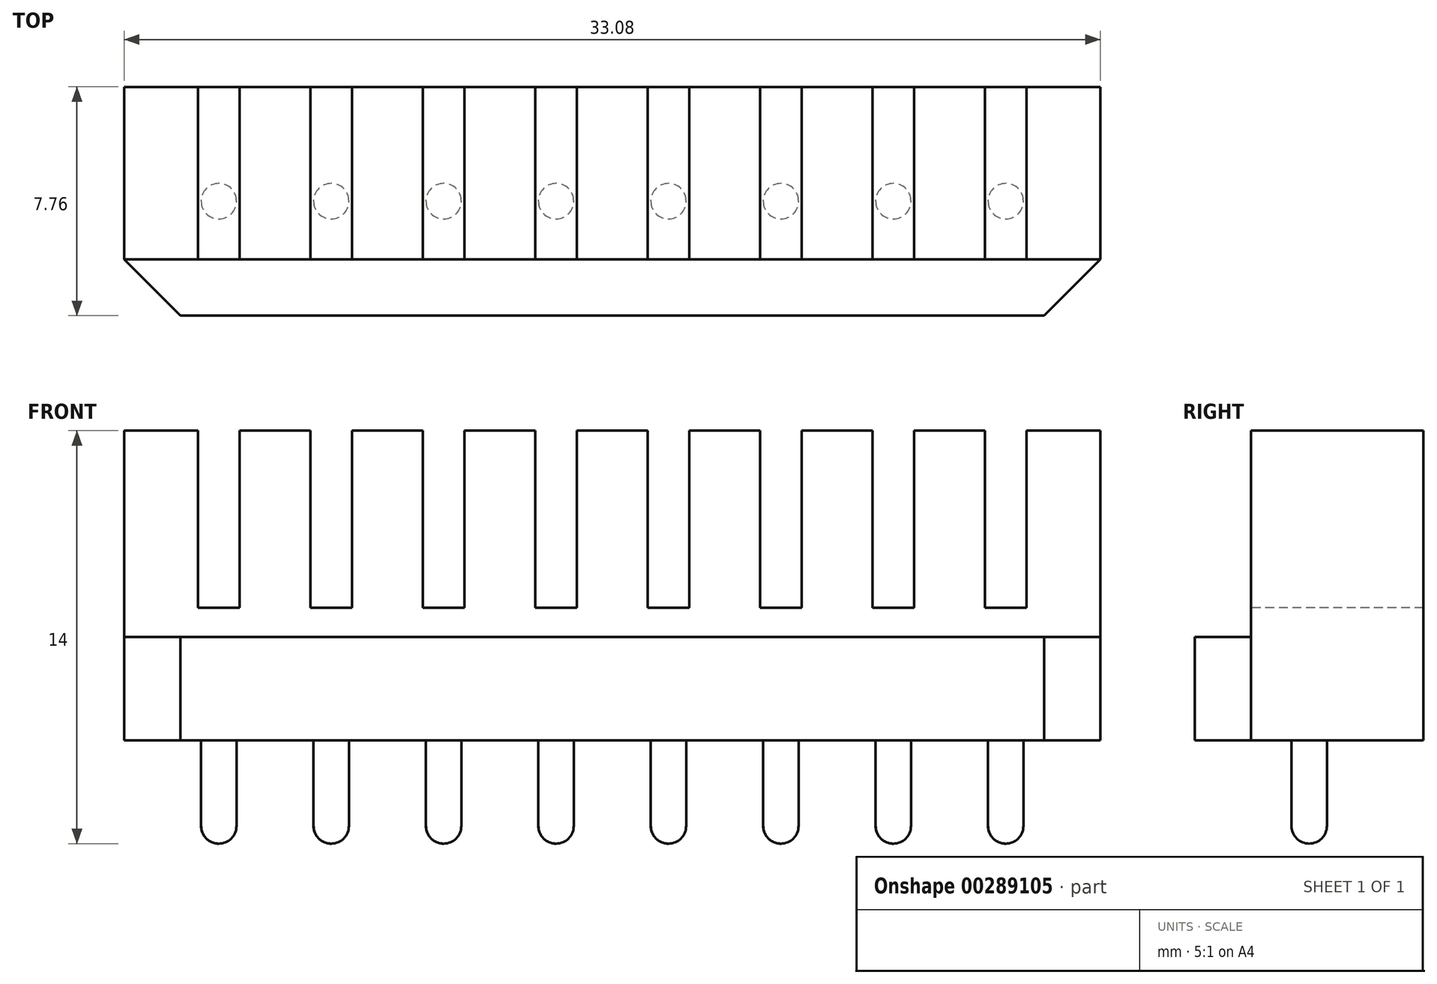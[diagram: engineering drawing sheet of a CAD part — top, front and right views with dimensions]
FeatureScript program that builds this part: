
annotation { "Feature Type Name" : "Feature", "Feature Type Description" : "" }
export const myFeature = defineFeature(function(context is Context, id is Id, definition is map)
    precondition{}
    {
        {
            var Q0;
            Q0=qCreatedBy(makeId("Top.planeOp"),FACE);
            var sketch = newSketch(context, id + "F0", { "sketchPlane" : qUnion([Q0])});
            skLineSegment(sketch, "E0.bottom", {"start": v(-16.54, 3.88) * mm, "end": v(16.54, 3.88) * mm});
            skLineSegment(sketch, "E0.top", {"start": v(-16.54, -3.87) * mm, "end": v(16.54, -3.87) * mm});
            skLineSegment(sketch, "E0.left", {"start": v(-16.54, 3.88) * mm, "end": v(-16.54, -3.88) * mm});
            skLineSegment(sketch, "E0.right", {"start": v(16.54, 3.88) * mm, "end": v(16.54, -3.87) * mm});
            skPoint(sketch, "E0.middle", {"position": v(0, 0) * mm});
            skSolve(sketch);
        }
        {
            var Q0;
            Q0 = qSketchRegion(id + "F0", true);
            extrude(context, id + "F1", {"entities" : qUnion([Q0]), "depth" : 3.5 * mm, "offsetDistance" : 25 * mm});
        }
        {
            var Q0;
            Q0=makeQuery(id+"F1.opExtrude","CAP_FACE",FACE,{"disambiguationData":[OSD([sQuery(id+"F0.wireOp",EDGE,"E0.bottom"),sQuery(id+"F0.wireOp",EDGE,"E0.top"),sQuery(id+"F0.wireOp",EDGE,"E0.left"),sQuery(id+"F0.wireOp",EDGE,"E0.right")])],"isStart":false});
            var sketch = newSketch(context, id + "F2", { "sketchPlane" : qUnion([Q0])});
            skLineSegment(sketch, "E1.bottom", {"start": v(-16.54, 3.88) * mm, "end": v(16.54, 3.88) * mm});
            skLineSegment(sketch, "E1.top", {"start": v(-16.54, -1.97) * mm, "end": v(16.54, -1.97) * mm});
            skLineSegment(sketch, "E1.left", {"start": v(-16.54, 3.88) * mm, "end": v(-16.54, -1.97) * mm});
            skLineSegment(sketch, "E1.right", {"start": v(16.54, 3.88) * mm, "end": v(16.54, -1.97) * mm});
            skSolve(sketch);
        }
        {
            var Q0;
            Q0 = qSketchRegion(id + "F2", true);
            extrude(context, id + "F3", {"entities" : qUnion([Q0]), "operationType" : NewBodyOperationType.ADD, "depth" : 7 * mm, "offsetDistance" : 25 * mm});
        }
        {
            var Q0;
            Q0=makeQuery(id+"F1.opExtrude","SWEPT_EDGE",EDGE,{"disambiguationData":[OSD([sQuery(id+"F0.wireOp",EDGE,"E0.top"),sQuery(id+"F0.wireOp",EDGE,"E0.right")])]});
            var Q1;
            Q1=makeQuery(id+"F1.opExtrude","SWEPT_EDGE",EDGE,{"disambiguationData":[OSD([sQuery(id+"F0.wireOp",EDGE,"E0.top"),sQuery(id+"F0.wireOp",EDGE,"E0.left")])]});
            chamfer(context, id + "F4", {"entities" : qUnion([Q0, Q1]), "width" : 1.9 * mm, "tangentPropagation" : true});
        }
        {
            var Q0;
            Q0=makeQuery(id+"F3.opExtrude","CAP_FACE",FACE,{"disambiguationData":[OSD([sQuery(id+"F2.wireOp",EDGE,"E1.bottom"),sQuery(id+"F2.wireOp",EDGE,"E1.top"),sQuery(id+"F2.wireOp",EDGE,"E1.left"),sQuery(id+"F2.wireOp",EDGE,"E1.right")])],"isStart":false});
            var sketch = newSketch(context, id + "F5", { "sketchPlane" : qUnion([Q0])});
            skLineSegment(sketch, "E2.bottom", {"start": v(-14.03, 3.88) * mm, "end": v(-12.63, 3.88) * mm});
            skLineSegment(sketch, "E2.top", {"start": v(-14.03, -1.97) * mm, "end": v(-12.63, -1.97) * mm});
            skLineSegment(sketch, "E2.left", {"start": v(-14.03, 3.88) * mm, "end": v(-14.03, -1.97) * mm});
            skLineSegment(sketch, "E2.right", {"start": v(-12.63, 3.88) * mm, "end": v(-12.63, -1.97) * mm});
            skLineSegment(sketch, "E3.1.0.0", {"start": v(-10.22, 3.88) * mm, "end": v(-8.82, 3.88) * mm});
            skLineSegment(sketch, "E3.1.0.1", {"start": v(-8.82, 3.88) * mm, "end": v(-8.82, -1.97) * mm});
            skLineSegment(sketch, "E3.1.0.2", {"start": v(-10.22, 3.88) * mm, "end": v(-10.22, -1.97) * mm});
            skLineSegment(sketch, "E3.1.0.3", {"start": v(-10.22, -1.97) * mm, "end": v(-8.82, -1.97) * mm});
            skLineSegment(sketch, "E3.2.0.0", {"start": v(-6.41, 3.88) * mm, "end": v(-5.01, 3.88) * mm});
            skLineSegment(sketch, "E3.2.0.1", {"start": v(-5.01, 3.88) * mm, "end": v(-5.01, -1.97) * mm});
            skLineSegment(sketch, "E3.2.0.2", {"start": v(-6.41, 3.88) * mm, "end": v(-6.41, -1.97) * mm});
            skLineSegment(sketch, "E3.2.0.3", {"start": v(-6.41, -1.97) * mm, "end": v(-5.01, -1.97) * mm});
            skLineSegment(sketch, "E3.3.0.0", {"start": v(-2.6, 3.88) * mm, "end": v(-1.2, 3.88) * mm});
            skLineSegment(sketch, "E3.3.0.1", {"start": v(-1.2, 3.88) * mm, "end": v(-1.2, -1.97) * mm});
            skLineSegment(sketch, "E3.3.0.2", {"start": v(-2.6, 3.88) * mm, "end": v(-2.6, -1.97) * mm});
            skLineSegment(sketch, "E3.3.0.3", {"start": v(-2.6, -1.97) * mm, "end": v(-1.2, -1.97) * mm});
            skLineSegment(sketch, "E3.4.0.0", {"start": v(1.2, 3.88) * mm, "end": v(2.6, 3.88) * mm});
            skLineSegment(sketch, "E3.4.0.1", {"start": v(2.6, 3.88) * mm, "end": v(2.6, -1.97) * mm});
            skLineSegment(sketch, "E3.4.0.2", {"start": v(1.2, 3.88) * mm, "end": v(1.2, -1.97) * mm});
            skLineSegment(sketch, "E3.4.0.3", {"start": v(1.2, -1.97) * mm, "end": v(2.6, -1.97) * mm});
            skLineSegment(sketch, "E3.5.0.0", {"start": v(5.02, 3.88) * mm, "end": v(6.42, 3.88) * mm});
            skLineSegment(sketch, "E3.5.0.1", {"start": v(6.42, 3.88) * mm, "end": v(6.42, -1.97) * mm});
            skLineSegment(sketch, "E3.5.0.2", {"start": v(5.02, 3.88) * mm, "end": v(5.02, -1.97) * mm});
            skLineSegment(sketch, "E3.5.0.3", {"start": v(5.02, -1.97) * mm, "end": v(6.42, -1.97) * mm});
            skLineSegment(sketch, "E3.6.0.0", {"start": v(8.82, 3.88) * mm, "end": v(10.22, 3.88) * mm});
            skLineSegment(sketch, "E3.6.0.1", {"start": v(10.22, 3.88) * mm, "end": v(10.22, -1.97) * mm});
            skLineSegment(sketch, "E3.6.0.2", {"start": v(8.82, 3.88) * mm, "end": v(8.82, -1.97) * mm});
            skLineSegment(sketch, "E3.6.0.3", {"start": v(8.82, -1.97) * mm, "end": v(10.22, -1.97) * mm});
            skLineSegment(sketch, "E3.7.0.0", {"start": v(12.63, 3.88) * mm, "end": v(14.03, 3.88) * mm});
            skLineSegment(sketch, "E3.7.0.1", {"start": v(14.03, 3.88) * mm, "end": v(14.03, -1.97) * mm});
            skLineSegment(sketch, "E3.7.0.2", {"start": v(12.63, 3.88) * mm, "end": v(12.63, -1.97) * mm});
            skLineSegment(sketch, "E3.7.0.3", {"start": v(12.63, -1.97) * mm, "end": v(14.03, -1.97) * mm});
            skLineSegment(sketch, "E3.direction1", {"start": v(-14.03, -1.97) * mm, "end": v(-10.22, -1.97) * mm, "construction": true});
            skLineSegment(sketch, "E4", {"start": v(-1.2, 0) * mm, "end": v(1.2, 0) * mm, "construction": true});
            skSolve(sketch);
        }
        {
            var Q0;
            Q0 = qSketchRegion(id + "F5", true);
            extrude(context, id + "F6", {"entities" : qUnion([Q0]), "operationType" : NewBodyOperationType.REMOVE, "oppositeDirection" : true, "depth" : 6 * mm, "offsetDistance" : 25 * mm});
        }
        {
            var Q0;
            Q0=makeQuery(id+"F1.opExtrude","CAP_FACE",FACE,{"disambiguationData":[OSD([sQuery(id+"F0.wireOp",EDGE,"E0.bottom"),sQuery(id+"F0.wireOp",EDGE,"E0.top"),sQuery(id+"F0.wireOp",EDGE,"E0.left"),sQuery(id+"F0.wireOp",EDGE,"E0.right")])],"isStart":true});
            var sketch = newSketch(context, id + "F7", { "sketchPlane" : qUnion([Q0])});
            skCircle(sketch, "E5", {"center": v(-13.34, 0) * mm, "radius": 0.6 * mm});
            skCircle(sketch, "E6.1.0.0", {"center": v(-9.53, 0) * mm, "radius": 0.6 * mm});
            skCircle(sketch, "E6.2.0.0", {"center": v(-5.72, 0) * mm, "radius": 0.6 * mm});
            skCircle(sketch, "E6.3.0.0", {"center": v(-1.9, 0) * mm, "radius": 0.6 * mm});
            skCircle(sketch, "E6.4.0.0", {"center": v(1.9, 0) * mm, "radius": 0.6 * mm});
            skCircle(sketch, "E6.5.0.0", {"center": v(5.72, 0) * mm, "radius": 0.6 * mm});
            skCircle(sketch, "E6.6.0.0", {"center": v(9.53, 0) * mm, "radius": 0.6 * mm});
            skCircle(sketch, "E6.7.0.0", {"center": v(13.34, 0) * mm, "radius": 0.6 * mm});
            skLineSegment(sketch, "E6.direction1", {"start": v(-13.34, 0) * mm, "end": v(-9.53, 0) * mm, "construction": true});
            skLineSegment(sketch, "E7", {"start": v(-1.9, 0) * mm, "end": v(1.9, 0) * mm, "construction": true});
            skSolve(sketch);
        }
        {
            var Q0;
            Q0 = qSketchRegion(id + "F7", true);
            extrude(context, id + "F8", {"entities" : qUnion([Q0]), "depth" : 3.5 * mm, "offsetDistance" : 25 * mm});
        }
        {
            var Q0;
            Q0=makeQuery(id+"F8.opExtrude","CAP_FACE",FACE,{"disambiguationData":[OSD([sQuery(id+"F7.wireOp",EDGE,"E5")])],"isStart":false});
            var Q1;
            Q1=makeQuery(id+"F8.opExtrude","CAP_FACE",FACE,{"disambiguationData":[OSD([sQuery(id+"F7.wireOp",EDGE,"E6.1.0.0")])],"isStart":false});
            var Q2;
            Q2=makeQuery(id+"F8.opExtrude","CAP_FACE",FACE,{"disambiguationData":[OSD([sQuery(id+"F7.wireOp",EDGE,"E6.2.0.0")])],"isStart":false});
            var Q3;
            Q3=makeQuery(id+"F8.opExtrude","CAP_FACE",FACE,{"disambiguationData":[OSD([sQuery(id+"F7.wireOp",EDGE,"E6.3.0.0")])],"isStart":false});
            var Q4;
            Q4=makeQuery(id+"F8.opExtrude","CAP_FACE",FACE,{"disambiguationData":[OSD([sQuery(id+"F7.wireOp",EDGE,"E6.4.0.0")])],"isStart":false});
            var Q5;
            Q5=makeQuery(id+"F8.opExtrude","CAP_FACE",FACE,{"disambiguationData":[OSD([sQuery(id+"F7.wireOp",EDGE,"E6.5.0.0")])],"isStart":false});
            var Q6;
            Q6=makeQuery(id+"F8.opExtrude","CAP_FACE",FACE,{"disambiguationData":[OSD([sQuery(id+"F7.wireOp",EDGE,"E6.6.0.0")])],"isStart":false});
            var Q7;
            Q7=makeQuery(id+"F8.opExtrude","CAP_FACE",FACE,{"disambiguationData":[OSD([sQuery(id+"F7.wireOp",EDGE,"E6.7.0.0")])],"isStart":false});
            fillet(context, id + "F9", {"entities" : qUnion([Q0, Q1, Q2, Q3, Q4, Q5, Q6, Q7]), "radius" : 0.6 * mm, "tangentPropagation" : true, "allowEdgeOverflow" : false});
        }
    });
